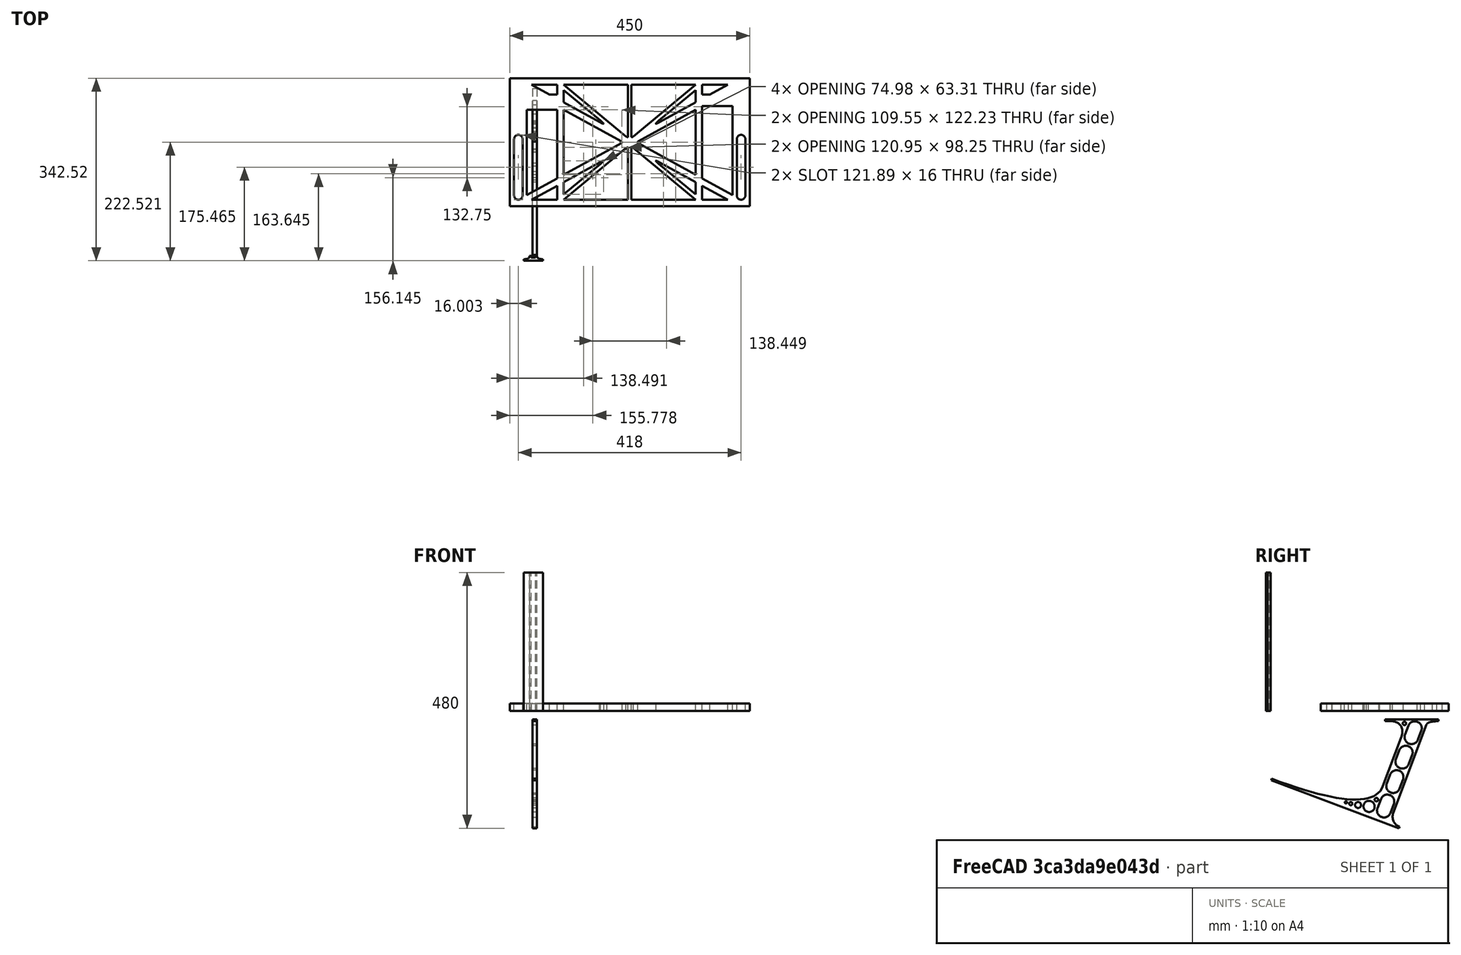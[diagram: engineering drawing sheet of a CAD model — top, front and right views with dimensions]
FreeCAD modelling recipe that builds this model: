
FCSTD DOCUMENT  (FreeCAD 0.19R0.19.2)
Label: laptopStand068
License: All rights reserved
LicenseURL: http://en.wikipedia.org/wiki/All_rights_reserved
objects: Sketcher::SketchObject×3, Part::Extrusion×3
note: 6 computed .brp shape members not serialized (recipe doc carries the construction recipe); baked Part::Feature solids carry a one-line shape summary decoded from their .brp

FEATURE [Sketcher::SketchObject] Sketch
  FullyConstrained = true
  sketch-geometry (126):
    g0: LineSegment StartX=-10.9272 StartY=-82.7794 StartZ=0 EndX=46.0728 EndY=-51.4823 EndZ=0
    g1: LineSegment StartX=366.073 StartY=-91.7794 StartZ=0 EndX=318.073 EndY=-65.424 EndZ=0
    g2: LineSegment StartX=-10.9272 StartY=77.3346 StartZ=0 EndX=-10.9272 EndY=-82.7794 EndZ=0
    g3: LineSegment StartX=375.073 StartY=-82.7794 StartZ=0 EndX=375.073 EndY=83.9235 EndZ=0
    g4: LineSegment StartX=-1.92719 StartY=-91.7794 StartZ=0 EndX=46.0728 EndY=-91.7794 EndZ=0
    g5: LineSegment StartX=318.073 StartY=124.221 StartZ=0 EndX=366.073 EndY=124.221 EndZ=0
    g6: LineSegment StartX=306.073 StartY=124.221 StartZ=0 EndX=189.124 EndY=27.0628 EndZ=0
    g7: LineSegment StartX=58.0728 StartY=-91.7794 StartZ=0 EndX=175.022 EndY=5.37834 EndZ=0
    g8: LineSegment StartX=58.0728 StartY=-81.8102 StartZ=0 EndX=58.0728 EndY=-58.8351 EndZ=0
    g9: LineSegment StartX=306.073 StartY=114.251 StartZ=0 EndX=306.073 EndY=91.2763 EndZ=0
    g10: LineSegment StartX=175.022 StartY=27.0628 StartZ=0 EndX=58.0728 EndY=124.221 EndZ=0
    g11: LineSegment StartX=139.632 StartY=-14.0532 StartZ=0 EndX=58.0728 EndY=-81.8102 EndZ=0
    g12: LineSegment StartX=139.632 StartY=-14.0532 StartZ=0 EndX=58.0728 EndY=-58.8351 EndZ=0
    g13: LineSegment StartX=189.124 StartY=5.37834 StartZ=0 EndX=306.073 EndY=-91.7794 EndZ=0
    g14: LineSegment StartX=306.073 StartY=77.3346 StartZ=0 EndX=306.073 EndY=-44.8935 EndZ=0
    g15: LineSegment StartX=318.073 StartY=83.9235 StartZ=0 EndX=318.073 EndY=-51.4823 EndZ=0
    g16: LineSegment StartX=306.073 StartY=-58.8351 StartZ=0 EndX=306.073 EndY=-81.8102 EndZ=0
    g17: LineSegment StartX=318.073 StartY=-51.4823 StartZ=0 EndX=375.073 EndY=-82.7794 EndZ=0
    g18: LineSegment StartX=318.073 StartY=-65.424 StartZ=0 EndX=318.073 EndY=-91.7794 EndZ=0
    g19: LineSegment StartX=318.073 StartY=-91.7794 StartZ=0 EndX=366.073 EndY=-91.7794 EndZ=0
    g20: LineSegment StartX=58.0728 StartY=-44.8935 StartZ=0 EndX=58.0728 EndY=77.3346 EndZ=0
    g21: LineSegment StartX=46.0728 StartY=-65.424 StartZ=0 EndX=-1.92719 EndY=-91.7794 EndZ=0
    g22: LineSegment StartX=46.0728 StartY=-65.424 StartZ=0 EndX=46.0728 EndY=-91.7794 EndZ=0
    g23: LineSegment StartX=58.0728 StartY=91.2763 StartZ=0 EndX=58.0728 EndY=114.251 EndZ=0
    g24: LineSegment StartX=46.0728 StartY=77.3346 StartZ=0 EndX=46.0728 EndY=-51.4823 EndZ=0
    g25: LineSegment StartX=-42.9272 StartY=136.221 StartZ=0 EndX=-42.9272 EndY=-103.779 EndZ=0
    g26: LineSegment StartX=407.073 StartY=136.221 StartZ=0 EndX=407.073 EndY=-103.779 EndZ=0
    g27: LineSegment StartX=179.022 StartY=27.0628 StartZ=0 EndX=179.022 EndY=124.221 EndZ=0
    g28: LineSegment StartX=185.124 StartY=27.0628 StartZ=0 EndX=185.124 EndY=124.221 EndZ=0
    g29: ArcOfCircle CenterX=-26.9272 CenterY=22.1087 CenterZ=0 NormalX=0 NormalY=0 NormalZ=1 AngleXU=0 Radius=8 StartAngle=1e-16 EndAngle=3.14159
    g30: ArcOfCircle CenterX=-26.9272 CenterY=-83.7794 CenterZ=0 NormalX=0 NormalY=0 NormalZ=1 AngleXU=0 Radius=8 StartAngle=3.14159 EndAngle=6.28319
    g31: LineSegment StartX=-34.9272 StartY=22.1087 StartZ=0 EndX=-34.9272 EndY=-83.7794 EndZ=0
    g32: LineSegment StartX=-18.9272 StartY=22.1087 StartZ=0 EndX=-18.9272 EndY=-83.7794 EndZ=0
    g33: LineSegment StartX=185.124 StartY=-91.7794 StartZ=0 EndX=306.073 EndY=-91.7794 EndZ=0
    g34: LineSegment StartX=179.022 StartY=-91.7794 StartZ=0 EndX=58.0728 EndY=-91.7794 EndZ=0
    g35: LineSegment StartX=306.073 StartY=124.221 StartZ=0 EndX=185.124 EndY=124.221 EndZ=0
    g36: LineSegment StartX=179.022 StartY=124.221 StartZ=0 EndX=58.0728 EndY=124.221 EndZ=0
    g37: ArcOfCircle CenterX=391.073 CenterY=22.1087 CenterZ=0 NormalX=0 NormalY=0 NormalZ=1 AngleXU=0 Radius=8 StartAngle=-4.4e-15 EndAngle=3.14159
    g38: LineSegment StartX=399.073 StartY=22.1087 StartZ=0 EndX=399.073 EndY=-83.7794 EndZ=0
    g39: LineSegment StartX=383.073 StartY=22.1087 StartZ=0 EndX=383.073 EndY=-83.7794 EndZ=0
    g40: ArcOfCircle CenterX=391.073 CenterY=-83.7794 CenterZ=0 NormalX=0 NormalY=0 NormalZ=1 AngleXU=0 Radius=8 StartAngle=3.14159 EndAngle=6.28319
    g41: Circle CenterX=175.022 CenterY=27.0628 CenterZ=0 NormalX=0 NormalY=0 NormalZ=1 AngleXU=0 Radius=1
    g42: Circle CenterX=179.022 CenterY=24.8665 CenterZ=0 NormalX=0 NormalY=0 NormalZ=1 AngleXU=0 Radius=1
    g43: Circle CenterX=179.022 CenterY=27.0628 CenterZ=0 NormalX=0 NormalY=0 NormalZ=1 AngleXU=0 Radius=1
    g44: BSplineCurve PolesCount=3 KnotsCount=2 Degree=2 IsPeriodic=0
    g45: GeomPoint X=175.022 Y=27.0628 Z=0
    g46: GeomPoint X=179.022 Y=27.0628 Z=0
    g47: Circle CenterX=189.124 CenterY=27.0628 CenterZ=0 NormalX=0 NormalY=0 NormalZ=1 AngleXU=0 Radius=1
    g48: Circle CenterX=185.124 CenterY=24.8665 CenterZ=0 NormalX=0 NormalY=0 NormalZ=1 AngleXU=0 Radius=1
    g49: Circle CenterX=185.124 CenterY=27.0628 CenterZ=0 NormalX=0 NormalY=0 NormalZ=1 AngleXU=0 Radius=1
    g50: BSplineCurve PolesCount=3 KnotsCount=2 Degree=2 IsPeriodic=0
    g51: GeomPoint X=189.124 Y=27.0628 Z=0
    g52: GeomPoint X=185.124 Y=27.0628 Z=0
    g53: Circle CenterX=175.022 CenterY=5.37834 CenterZ=0 NormalX=0 NormalY=0 NormalZ=1 AngleXU=0 Radius=1
    g54: Circle CenterX=179.022 CenterY=7.57463 CenterZ=0 NormalX=0 NormalY=0 NormalZ=1 AngleXU=0 Radius=1
    g55: Circle CenterX=179.022 CenterY=5.34704 CenterZ=0 NormalX=0 NormalY=0 NormalZ=1 AngleXU=0 Radius=1
    g56: BSplineCurve PolesCount=3 KnotsCount=2 Degree=2 IsPeriodic=0
    g57: GeomPoint X=175.022 Y=5.37834 Z=0
    g58: GeomPoint X=179.022 Y=5.34704 Z=0
    g59: Circle CenterX=189.124 CenterY=5.37834 CenterZ=0 NormalX=0 NormalY=0 NormalZ=1 AngleXU=0 Radius=1
    g60: Circle CenterX=185.124 CenterY=7.57463 CenterZ=0 NormalX=0 NormalY=0 NormalZ=1 AngleXU=0 Radius=1
    g61: Circle CenterX=185.124 CenterY=5.34704 CenterZ=0 NormalX=0 NormalY=0 NormalZ=1 AngleXU=0 Radius=1
    g62: BSplineCurve PolesCount=3 KnotsCount=2 Degree=2 IsPeriodic=0
    g63: GeomPoint X=189.124 Y=5.37834 Z=0
    g64: GeomPoint X=185.124 Y=5.34704 Z=0
    g65: LineSegment StartX=179.022 StartY=5.34704 StartZ=0 EndX=179.022 EndY=-91.7794 EndZ=0
    g66: LineSegment StartX=185.124 StartY=-91.7794 StartZ=0 EndX=185.124 EndY=5.34704 EndZ=0
    g67: Circle CenterX=165.871 CenterY=18.1458 CenterZ=0 NormalX=0 NormalY=0 NormalZ=1 AngleXU=0 Radius=1
    g68: Circle CenterX=169.377 CenterY=16.2206 CenterZ=0 NormalX=0 NormalY=0 NormalZ=1 AngleXU=0 Radius=1
    g69: Circle CenterX=165.871 CenterY=14.2954 CenterZ=0 NormalX=0 NormalY=0 NormalZ=1 AngleXU=0 Radius=1
    g70: BSplineCurve PolesCount=3 KnotsCount=2 Degree=2 IsPeriodic=0
    g71: GeomPoint X=165.871 Y=18.1458 Z=0
    g72: GeomPoint X=165.871 Y=14.2954 Z=0
    g73: Circle CenterX=198.275 CenterY=18.1458 CenterZ=0 NormalX=0 NormalY=0 NormalZ=1 AngleXU=0 Radius=1
    g74: Circle CenterX=194.768 CenterY=16.2206 CenterZ=0 NormalX=0 NormalY=0 NormalZ=1 AngleXU=0 Radius=1
    g75: Circle CenterX=198.275 CenterY=14.2954 CenterZ=0 NormalX=0 NormalY=0 NormalZ=1 AngleXU=0 Radius=1
    g76: BSplineCurve PolesCount=3 KnotsCount=2 Degree=2 IsPeriodic=0
    g77: GeomPoint X=198.275 Y=18.1458 Z=0
    g78: GeomPoint X=198.275 Y=14.2954 Z=0
    g79: LineSegment StartX=165.871 StartY=18.1458 StartZ=0 EndX=58.0728 EndY=77.3346 EndZ=0
    g80: LineSegment StartX=58.0728 StartY=-44.8935 StartZ=0 EndX=165.871 EndY=14.2954 EndZ=0
    g81: LineSegment StartX=198.275 StartY=18.1458 StartZ=0 EndX=306.073 EndY=77.3346 EndZ=0
    g82: LineSegment StartX=198.275 StartY=14.2954 StartZ=0 EndX=306.073 EndY=-44.8935 EndZ=0
    g83: LineSegment StartX=407.073 StartY=-103.779 StartZ=0 EndX=-42.9272 EndY=-103.779 EndZ=0
    g84: LineSegment StartX=407.073 StartY=136.221 StartZ=0 EndX=-42.9272 EndY=136.221 EndZ=0
    g85: LineSegment StartX=46.0728 StartY=77.3346 StartZ=0 EndX=-10.9272 EndY=77.3346 EndZ=0
    g86: LineSegment StartX=46.0728 StartY=105.865 StartZ=0 EndX=31.5028 EndY=105.865 EndZ=0
    g87: LineSegment StartX=46.0728 StartY=124.221 StartZ=0 EndX=46.0728 EndY=105.865 EndZ=0
    g88: LineSegment StartX=-1.92719 StartY=124.221 StartZ=0 EndX=31.5028 EndY=105.865 EndZ=0
    g89: LineSegment StartX=46.0728 StartY=124.221 StartZ=0 EndX=-1.92719 EndY=124.221 EndZ=0
    g90: LineSegment StartX=318.073 StartY=83.9235 StartZ=0 EndX=375.073 EndY=83.9235 EndZ=0
    g91: LineSegment StartX=318.073 StartY=105.865 StartZ=0 EndX=332.643 EndY=105.865 EndZ=0
    g92: LineSegment StartX=332.643 StartY=105.865 StartZ=0 EndX=366.073 EndY=124.221 EndZ=0
    g93: LineSegment StartX=318.073 StartY=124.221 StartZ=0 EndX=318.073 EndY=105.865 EndZ=0
    g94: Circle CenterX=125.607 CenterY=54.1951 CenterZ=0 NormalX=0 NormalY=0 NormalZ=1 AngleXU=0 Radius=1
    g95: Circle CenterX=139.632 CenterY=46.4944 CenterZ=0 NormalX=0 NormalY=0 NormalZ=1 AngleXU=0 Radius=1
    g96: Circle CenterX=127.325 CenterY=56.7187 CenterZ=0 NormalX=0 NormalY=0 NormalZ=1 AngleXU=0 Radius=1
    g97: BSplineCurve PolesCount=3 KnotsCount=2 Degree=2 IsPeriodic=0
    g98: GeomPoint X=125.607 Y=54.1951 Z=0
    g99: GeomPoint X=127.325 Y=56.7187 Z=0
    g100: LineSegment StartX=127.325 StartY=56.7187 StartZ=0 EndX=58.0728 EndY=114.251 EndZ=0
    g101: LineSegment StartX=58.0728 StartY=91.2763 StartZ=0 EndX=125.607 EndY=54.1951 EndZ=0
    g102: Circle CenterX=236.821 CenterY=56.7187 CenterZ=0 NormalX=0 NormalY=0 NormalZ=1 AngleXU=0 Radius=1
    g103: Circle CenterX=224.513 CenterY=46.4944 CenterZ=0 NormalX=0 NormalY=0 NormalZ=1 AngleXU=0 Radius=1
    g104: Circle CenterX=238.538 CenterY=54.1951 CenterZ=0 NormalX=0 NormalY=0 NormalZ=1 AngleXU=0 Radius=1
    g105: BSplineCurve PolesCount=3 KnotsCount=2 Degree=2 IsPeriodic=0
    g106: GeomPoint X=236.821 Y=56.7187 Z=0
    g107: GeomPoint X=238.538 Y=54.1951 Z=0
    g108: LineSegment StartX=236.821 StartY=56.7187 StartZ=0 EndX=306.073 EndY=114.251 EndZ=0
    g109: LineSegment StartX=238.538 StartY=54.1951 StartZ=0 EndX=306.073 EndY=91.2763 EndZ=0
    g110: Circle CenterX=238.538 CenterY=-21.7539 CenterZ=0 NormalX=0 NormalY=0 NormalZ=1 AngleXU=0 Radius=1
    g111: Circle CenterX=224.513 CenterY=-14.0532 CenterZ=0 NormalX=0 NormalY=0 NormalZ=1 AngleXU=0 Radius=1
    g112: Circle CenterX=236.821 CenterY=-24.2775 CenterZ=0 NormalX=0 NormalY=0 NormalZ=1 AngleXU=0 Radius=1
    g113: BSplineCurve PolesCount=3 KnotsCount=2 Degree=2 IsPeriodic=0
    g114: GeomPoint X=238.538 Y=-21.7539 Z=0
    g115: GeomPoint X=236.821 Y=-24.2775 Z=0
    g116: LineSegment StartX=238.538 StartY=-21.7539 StartZ=0 EndX=306.073 EndY=-58.8351 EndZ=0
    g117: LineSegment StartX=236.821 StartY=-24.2775 StartZ=0 EndX=306.073 EndY=-81.8102 EndZ=0
    g118: LineSegment StartX=139.632 StartY=-14.0532 StartZ=0 EndX=125.607 EndY=-21.7539 EndZ=0
    g119: LineSegment StartX=139.632 StartY=-14.0532 StartZ=0 EndX=127.325 EndY=-24.2775 EndZ=0
    g120: Circle CenterX=125.607 CenterY=-21.7539 CenterZ=0 NormalX=0 NormalY=0 NormalZ=1 AngleXU=0 Radius=1
    g121: Circle CenterX=139.632 CenterY=-14.0532 CenterZ=0 NormalX=0 NormalY=0 NormalZ=1 AngleXU=0 Radius=1
    g122: Circle CenterX=127.325 CenterY=-24.2775 CenterZ=0 NormalX=0 NormalY=0 NormalZ=1 AngleXU=0 Radius=1
    g123: BSplineCurve PolesCount=3 KnotsCount=2 Degree=2 IsPeriodic=0
    g124: GeomPoint X=125.607 Y=-21.7539 Z=0
    g125: GeomPoint X=127.325 Y=-24.2775 Z=0
  constraints (233):
    c: Horizontal(g4)
    c: Horizontal(g5)
    c: Coincident(g12,g11)
    c: Tangent(g9,g14)
    c: Tangent(g14,g16)
    c: Coincident(g15,g17)
    c: Coincident(g18,g1)
    c: Tangent(g15,g18)
    c: Coincident(g11,g8)
    c: Tangent(g8,g20)
    c: Coincident(g12,g8)
    c: Tangent(g12,g21)
    c: Coincident(g22,g21)
    c: Coincident(g0,g24)
    c: Tangent(g20,g23)
    c: Block(g10)
    c: Block(g6)
    c: Block(g17)
    c: Block(g3)
    c: Block(g16)
    c: Block(g1)
    c: Block(g18)
    c: Block(g13)
    c: Block(g7)
    c: Block(g12)
    c: Block(g11)
    c: Block(g22)
    c: Block(g21)
    c: Block(g0)
    c: Block(g2)
    c: Block(g23)
    c: Block(g14)
    c: Block(g5)
    c: Block(g19)
    c: Block(g4)
    c: Vertical(g25)
    c: Vertical(g26)
    c: Block(g26)
    c: Block(g25)
    c: Vertical(g27)
    c: Vertical(g28)
    c: Block(g27)
    c: Block(g28)
    c: Tangent(g29,g32) = 1.5708
    c: Tangent(g29,g31) = -1.5708
    c: Tangent(g31,g30) = -1.5708
    c: Tangent(g32,g30) = 1.5708
    c: Vertical(g31)
    c: Equal(g29,g30)
    c: Block(g32)
    c: Block(g31)
    c: Coincident(g33,g13)
    c: Horizontal(g33)
    c: Coincident(g34,g7)
    c: Horizontal(g34)
    c: Coincident(g35,g6)
    c: Coincident(g35,g28)
    c: Horizontal(g35)
    c: Coincident(g36,g27)
    c: Coincident(g36,g10)
    c: Horizontal(g36)
    c: Tangent(g37,g38) = 1.5708
    c: Tangent(g38,g40) = 1.5708
    c: Equal(g37,g40)
    c: Coincident(g39,g37)
    c: Coincident(g39,g40)
    c: Block(g38)
    c: Block(g39)
    c: Coincident(g44,g10)
    c: Weight(g41) = 1
    c: Equal(g41,g42)
    c: Equal(g41,g43)
    c: Coincident(g44,g27)
    c: InternalAlignment(g41,g44)
    c: InternalAlignment(g42,g44)
    c: InternalAlignment(g43,g44)
    c: InternalAlignment(g45,g44)
    c: InternalAlignment(g46,g44)
    c: Coincident(g50,g6)
    c: Weight(g47) = 1
    c: Equal(g47,g48)
    c: Equal(g47,g49)
    c: Coincident(g50,g28)
    c: InternalAlignment(g47,g50)
    c: InternalAlignment(g48,g50)
    c: InternalAlignment(g49,g50)
    c: InternalAlignment(g51,g50)
    c: InternalAlignment(g52,g50)
    c: Block(g50)
    c: Block(g44)
    c: Coincident(g56,g7)
    c: Weight(g53) = 1
    c: Equal(g53,g54)
    c: Equal(g53,g55)
    c: InternalAlignment(g53,g56)
    c: InternalAlignment(g54,g56)
    c: InternalAlignment(g55,g56)
    c: InternalAlignment(g57,g56)
    c: InternalAlignment(g58,g56)
    c: Weight(g59) = 1
    c: Equal(g59,g60)
    c: Equal(g59,g61)
    c: InternalAlignment(g59,g62)
    c: InternalAlignment(g60,g62)
    c: InternalAlignment(g61,g62)
    c: InternalAlignment(g63,g62)
    c: InternalAlignment(g64,g62)
    c: Block(g62)
    c: Block(g56)
    c: Coincident(g65,g56)
    c: Coincident(g65,g34)
    c: Vertical(g65)
    c: Coincident(g66,g33)
    c: Coincident(g66,g62)
    c: Vertical(g66)
    c: Weight(g67) = 1
    c: Equal(g67,g68)
    c: Equal(g67,g69)
    c: InternalAlignment(g67,g70)
    c: InternalAlignment(g68,g70)
    c: InternalAlignment(g69,g70)
    c: InternalAlignment(g71,g70)
    c: InternalAlignment(g72,g70)
    c: Weight(g73) = 1
    c: Equal(g73,g74)
    c: Equal(g73,g75)
    c: InternalAlignment(g73,g76)
    c: InternalAlignment(g74,g76)
    c: InternalAlignment(g75,g76)
    c: InternalAlignment(g77,g76)
    c: InternalAlignment(g78,g76)
    c: Block(g70)
    c: Block(g76)
    c: Coincident(g79,g70)
    c: Coincident(g79,g20)
    c: Coincident(g80,g20)
    c: Coincident(g80,g70)
    c: Coincident(g81,g76)
    c: Coincident(g81,g14)
    c: Coincident(g82,g76)
    c: Coincident(g82,g14)
    c: Block(g20)
    c: Coincident(g83,g26)
    c: Coincident(g83,g25)
    c: Horizontal(g83)
    c: Distance(g83) = 450
    c: Coincident(g84,g26)
    c: Coincident(g84,g25)
    c: Horizontal(g84)
    c: Horizontal(g85)
    c: Coincident(g24,g85)
    c: Horizontal(g86)
    c: Vertical(g87)
    c: Block(g87)
    c: Block(g86)
    c: Block(g85)
    c: Distance(g87) = 18.3554
    c: Coincident(g89,g87)
    c: Coincident(g89,g88)
    c: Horizontal(g89)
    c: Block(g89)
    c: Block(g88)
    c: Coincident(g86,g88)
    c: Coincident(g2,g85)
    c: Coincident(g90,g15)
    c: Horizontal(g90)
    c: Horizontal(g91)
    c: Block(g90)
    c: Block(g9)
    c: Coincident(g92,g5)
    c: Coincident(g93,g5)
    c: Coincident(g93,g91)
    c: Vertical(g93)
    c: Block(g93)
    c: Coincident(g91,g92)
    c: Block(g92)
    c: Coincident(g3,g90)
    c: Weight(g94) = 1
    c: Equal(g94,g95)
    c: Equal(g94,g96)
    c: InternalAlignment(g94,g97)
    c: InternalAlignment(g95,g97)
    c: InternalAlignment(g96,g97)
    c: InternalAlignment(g98,g97)
    c: InternalAlignment(g99,g97)
    c: Block(g97)
    c: Coincident(g100,g97)
    c: Coincident(g100,g23)
    c: Coincident(g101,g23)
    c: Coincident(g101,g97)
    c: Weight(g102) = 1
    c: Equal(g102,g103)
    c: Equal(g102,g104)
    c: InternalAlignment(g102,g105)
    c: InternalAlignment(g103,g105)
    c: InternalAlignment(g104,g105)
    c: InternalAlignment(g106,g105)
    c: InternalAlignment(g107,g105)
    c: Block(g105)
    c: Coincident(g108,g105)
    c: Coincident(g108,g9)
    c: Coincident(g109,g105)
    c: Coincident(g109,g9)
    c: Weight(g110) = 1
    c: Equal(g110,g111)
    c: Equal(g110,g112)
    c: InternalAlignment(g110,g113)
    c: InternalAlignment(g111,g113)
    c: InternalAlignment(g112,g113)
    c: InternalAlignment(g114,g113)
    c: InternalAlignment(g115,g113)
    c: Block(g113)
    c: Coincident(g116,g113)
    c: Coincident(g116,g16)
    c: Coincident(g117,g113)
    c: Coincident(g117,g16)
    c: Distance(g118) = 16
    c: Coincident(g118,g11)
    c: Coincident(g119,g11)
    c: Distance(g119) = 16
    c: Parallel(g119,g11)
    c: Parallel(g12,g118)
    c: Coincident(g123,g118)
    c: Weight(g120) = 1
    c: Equal(g120,g121)
    c: Coincident(g121,g11)
    c: Equal(g120,g122)
    c: Coincident(g123,g119)
    c: InternalAlignment(g120,g123)
    c: InternalAlignment(g121,g123)
    c: InternalAlignment(g122,g123)
    c: InternalAlignment(g124,g123)
    c: InternalAlignment(g125,g123)
FEATURE [Sketcher::SketchObject] Sketch001
  FullyConstrained = true
  MapMode = 4
  Placement = pos=(0,0,0) rot=(0.57735,0.57735,0.57735;2.0944rad)
  Support = -> [Sketch]
  sketch-geometry (46):
    g0: BSplineCurve PolesCount=3 KnotsCount=2 Degree=2 IsPeriodic=0
    g1: ArcOfCircle CenterX=73.1223 CenterY=-32.291 CenterZ=0 NormalX=0 NormalY=0 NormalZ=1 AngleXU=0 Radius=13 StartAngle=5.92268 EndAngle=9.06428
    g2: ArcOfCircle CenterX=66.7816 CenterY=-49.1439 CenterZ=0 NormalX=0 NormalY=0 NormalZ=1 AngleXU=0 Radius=13 StartAngle=2.78068 EndAngle=5.92131
    g3: ArcOfCircle CenterX=55.9263 CenterY=-78.1807 CenterZ=0 NormalX=0 NormalY=0 NormalZ=1 AngleXU=0 Radius=13 StartAngle=5.92268 EndAngle=9.06428
    g4: ArcOfCircle CenterX=49.5884 CenterY=-95.0342 CenterZ=0 NormalX=0 NormalY=0 NormalZ=1 AngleXU=0 Radius=13 StartAngle=2.78068 EndAngle=5.92131
    g5: ArcOfCircle CenterX=38.7206 CenterY=-124.067 CenterZ=0 NormalX=0 NormalY=0 NormalZ=1 AngleXU=0 Radius=13 StartAngle=5.92268 EndAngle=9.06428
    g6: ArcOfCircle CenterX=32.3875 CenterY=-140.92 CenterZ=0 NormalX=0 NormalY=0 NormalZ=1 AngleXU=0 Radius=13 StartAngle=2.78068 EndAngle=5.92131
    g7: ArcOfCircle CenterX=21.4715 CenterY=-169.934 CenterZ=0 NormalX=0 NormalY=0 NormalZ=1 AngleXU=0 Radius=13 StartAngle=5.92268 EndAngle=9.06428
    g8: ArcOfCircle CenterX=15.1336 CenterY=-186.787 CenterZ=0 NormalX=0 NormalY=0 NormalZ=1 AngleXU=0 Radius=13 StartAngle=2.78068 EndAngle=5.92131
    g9-g12: Circle x4 (B-spline internal-alignment scaffolding for g13; pole/knot coordinates omitted)
    g13: BSplineCurve PolesCount=4 KnotsCount=2 Degree=3 IsPeriodic=0
    g14: GeomPoint X=28.8094 Y=-19.0875 Z=0
    g15: GeomPoint X=47.0443 Y=-50.4712 Z=0
    g16: Circle CenterX=53.5586 CenterY=-23.2695 CenterZ=0 NormalX=0 NormalY=0 NormalZ=1 AngleXU=0 Radius=3.24518
    g17: Circle CenterX=-195.441 CenterY=-127.082 CenterZ=0 NormalX=0 NormalY=0 NormalZ=1 AngleXU=0 Radius=1
    g18: Circle CenterX=-8.24091 CenterY=-197.481 CenterZ=0 NormalX=0 NormalY=0 NormalZ=1 AngleXU=0 Radius=1
    g19: Circle CenterX=12.8789 CenterY=-141.321 CenterZ=0 NormalX=0 NormalY=0 NormalZ=1 AngleXU=0 Radius=1
    g20: BSplineCurve PolesCount=3 KnotsCount=2 Degree=2 IsPeriodic=0
    g21: GeomPoint X=-195.441 Y=-127.082 Z=0
    g22: GeomPoint X=12.8789 Y=-141.321 Z=0
    g23: Circle CenterX=-12.8016 CenterY=-179.036 CenterZ=0 NormalX=0 NormalY=0 NormalZ=1 AngleXU=0 Radius=10.5072
    g24: Circle CenterX=0.933922 CenterY=-166.43 CenterZ=0 NormalX=0 NormalY=0 NormalZ=1 AngleXU=0 Radius=3.26661
    g25: Circle CenterX=-33.5518 CenterY=-176.44 CenterZ=0 NormalX=0 NormalY=0 NormalZ=1 AngleXU=0 Radius=5.64388
    g26: Circle CenterX=-47.2366 CenterY=-173.859 CenterZ=0 NormalX=0 NormalY=0 NormalZ=1 AngleXU=0 Radius=3.01653
    g27: Circle CenterX=-56.2595 CenterY=-171.456 CenterZ=0 NormalX=0 NormalY=0 NormalZ=1 AngleXU=0 Radius=2.12826
    g28: ArcOfCircle CenterX=51.2151 CenterY=-198.473 CenterZ=0 NormalX=0 NormalY=0 NormalZ=1 AngleXU=0 Radius=20 StartAngle=2.78189 EndAngle=4.35269
    g29: LineSegment StartX=32.4951 StartY=-191.433 StartZ=0 EndX=94.6578 EndY=-26.1352 EndZ=0
    g30: LineSegment StartX=43.1192 StartY=-220.001 StartZ=0 EndX=-196.497 EndY=-129.89 EndZ=0
    g31: LineSegment StartX=43.1192 StartY=-220.001 StartZ=0 EndX=44.1752 EndY=-217.193 EndZ=0
    g32: LineSegment StartX=117.223 StartY=-19.0875 StartZ=0 EndX=117.223 EndY=-16.0875 EndZ=0
    g33: LineSegment StartX=117.223 StartY=-16.0875 StartZ=0 EndX=17.2232 EndY=-16.0875 EndZ=0
    g34: LineSegment StartX=17.2232 StartY=-16.0875 StartZ=0 EndX=17.2232 EndY=-19.0875 EndZ=0
    g35: LineSegment StartX=28.8094 StartY=-19.0875 StartZ=0 EndX=17.2232 EndY=-19.0875 EndZ=0
    g36: LineSegment StartX=47.0443 StartY=-50.4712 StartZ=0 EndX=12.8789 EndY=-141.321 EndZ=0
    g37: LineSegment StartX=-195.441 StartY=-127.082 StartZ=0 EndX=-196.497 EndY=-129.89 EndZ=0
    g38: LineSegment StartX=85.2866 StartY=-36.8766 StartZ=0 EndX=78.9396 EndY=-53.7463 EndZ=0
    g39: LineSegment StartX=60.9579 StartY=-27.7053 StartZ=0 EndX=54.6191 EndY=-44.5532 EndZ=0
    g40: LineSegment StartX=68.0907 StartY=-82.7664 StartZ=0 EndX=61.7465 EndY=-99.6365 EndZ=0
    g41: LineSegment StartX=43.7619 StartY=-73.595 StartZ=0 EndX=37.426 EndY=-90.4435 EndZ=0
    g42: LineSegment StartX=50.885 StartY=-128.652 StartZ=0 EndX=44.5456 EndY=-145.522 EndZ=0
    g43: LineSegment StartX=26.5562 StartY=-119.481 StartZ=0 EndX=20.2251 EndY=-136.329 EndZ=0
    g44: LineSegment StartX=9.3071 StartY=-165.349 StartZ=0 EndX=2.97115 EndY=-182.197 EndZ=0
    g45: LineSegment StartX=33.6358 StartY=-174.52 StartZ=0 EndX=27.2917 EndY=-191.39 EndZ=0
  constraints (71):
    c: Block(g0)
    c: Block(g1)
    c: Block(g2)
    c: Block(g4)
    c: Block(g3)
    c: Block(g6)
    c: Block(g5)
    c: Block(g8)
    c: Block(g7)
    c: Weight(g9) = 1
    c: Equal(g9,g10)
    c: Equal(g9,g11)
    c: Equal(g9,g12)
    c: InternalAlignment(g9-g12 -> g13) x4
    c: InternalAlignment(g14,g13)
    c: InternalAlignment(g15,g13)
    c: Block(g16)
    c: Weight(g17) = 1
    c: Equal(g17,g18)
    c: Equal(g17,g19)
    c: InternalAlignment(g17,g20)
    c: InternalAlignment(g18,g20)
    c: InternalAlignment(g19,g20)
    c: InternalAlignment(g21,g20)
    c: InternalAlignment(g22,g20)
    c: Block(g20)
    c: Block(g23)
    c: Block(g24)
    c: Block(g25)
    c: Block(g26)
    c: Block(g27)
    c: Block(g28)
    c: Coincident(g29,g28)
    c: Coincident(g29,g0)
    c: Block(g13)
    c: Coincident(g31,g30)
    c: Coincident(g31,g28)
    c: Block(g31)
    c: Coincident(g32,g0)
    c: Vertical(g32)
    c: Coincident(g33,g32)
    c: Horizontal(g33)
    c: Coincident(g34,g33)
    c: Vertical(g34)
    c: Block(g33)
    c: Coincident(g35,g13)
    c: Coincident(g35,g34)
    c: Horizontal(g35)
    c: Coincident(g36,g13)
    c: Coincident(g36,g20)
    c: Coincident(g37,g20)
    c: Coincident(g37,g30)
    c: Block(g30)
    c: Coincident(g38,g1)
    c: Coincident(g38,g2)
    c: Coincident(g39,g1)
    c: Coincident(g39,g2)
    c: Coincident(g40,g3)
    c: Coincident(g40,g4)
    c: Coincident(g41,g3)
    c: Coincident(g41,g4)
    c: Coincident(g42,g5)
    c: Coincident(g42,g6)
    c: Coincident(g43,g5)
    c: Coincident(g43,g6)
    c: Coincident(g44,g7)
    c: Coincident(g44,g8)
    c: Coincident(g45,g7)
    c: Coincident(g45,g8)
    c: Distance(g30) = 256
    c: Distance(g33) = 100
FEATURE [Part::Extrusion] Extrude002
  Base = -> Sketch001
  Dir = (1,0,0)
  DirMode = 2
  FaceMakerClass = Part::FaceMakerBullseye
  LengthFwd = 8
  LengthRev = 0
  Solid = true
  Symmetric = false
FEATURE [Sketcher::SketchObject] Sketch002
  FullyConstrained = true
  sketch-geometry (20):
    g0: LineSegment StartX=-2.77179 StartY=-200.304 StartZ=0 EndX=5.22821 EndY=-200.304 EndZ=0
    g1: LineSegment StartX=5.22821 StartY=-200.304 StartZ=0 EndX=5.22821 EndY=-197.304 EndZ=0
    g2: LineSegment StartX=-2.77179 StartY=-200.304 StartZ=0 EndX=-2.77179 EndY=-197.304 EndZ=0
    g3: LineSegment StartX=5.22821 StartY=-197.304 StartZ=0 EndX=8.22821 EndY=-197.304 EndZ=0
    g4: LineSegment StartX=-2.77179 StartY=-197.304 StartZ=0 EndX=-5.77179 EndY=-197.304 EndZ=0
    g5: LineSegment StartX=19.2282 StartY=-203.304 StartZ=0 EndX=19.2282 EndY=-206.304 EndZ=0
    g6: LineSegment StartX=-16.7718 StartY=-203.304 StartZ=0 EndX=-16.7718 EndY=-206.304 EndZ=0
    g7: LineSegment StartX=-16.7718 StartY=-206.304 StartZ=0 EndX=19.2282 EndY=-206.304 EndZ=0
    g8: Circle CenterX=-16.7718 CenterY=-203.304 CenterZ=0 NormalX=0 NormalY=0 NormalZ=1 AngleXU=0 Radius=1
    g9: Circle CenterX=-5.77179 CenterY=-203.304 CenterZ=0 NormalX=0 NormalY=0 NormalZ=1 AngleXU=0 Radius=1
    g10: Circle CenterX=-5.77179 CenterY=-197.304 CenterZ=0 NormalX=0 NormalY=0 NormalZ=1 AngleXU=0 Radius=1
    g11: BSplineCurve PolesCount=3 KnotsCount=2 Degree=2 IsPeriodic=0
    g12: GeomPoint X=-16.7718 Y=-203.304 Z=0
    g13: GeomPoint X=-5.77179 Y=-197.304 Z=0
    g14: Circle CenterX=19.2282 CenterY=-203.304 CenterZ=0 NormalX=0 NormalY=0 NormalZ=1 AngleXU=0 Radius=1
    g15: Circle CenterX=8.22821 CenterY=-203.304 CenterZ=0 NormalX=0 NormalY=0 NormalZ=1 AngleXU=0 Radius=1
    g16: Circle CenterX=8.22821 CenterY=-197.304 CenterZ=0 NormalX=0 NormalY=0 NormalZ=1 AngleXU=0 Radius=1
    g17: BSplineCurve PolesCount=3 KnotsCount=2 Degree=2 IsPeriodic=0
    g18: GeomPoint X=19.2282 Y=-203.304 Z=0
    g19: GeomPoint X=8.22821 Y=-197.304 Z=0
  constraints (41):
    c: Horizontal(g0)
    c: Distance(g0) = 8
    c: Coincident(g1,g0)
    c: Vertical(g1)
    c: Distance(g1) = 3
    c: Coincident(g2,g0)
    c: Vertical(g2)
    c: Distance(g2) = 3
    c: Coincident(g3,g1)
    c: Horizontal(g3)
    c: Distance(g3) = 3
    c: Coincident(g4,g2)
    c: Horizontal(g4)
    c: Distance(g4) = 3
    c: Vertical(g5)
    c: Vertical(g6)
    c: Coincident(g7,g6)
    c: Coincident(g7,g5)
    c: Weight(g8) = 1
    c: Equal(g8,g9)
    c: Equal(g8,g10)
    c: Coincident(g11,g4)
    c: InternalAlignment(g8,g11)
    c: InternalAlignment(g9,g11)
    c: InternalAlignment(g10,g11)
    c: InternalAlignment(g12,g11)
    c: InternalAlignment(g13,g11)
    c: Coincident(g17,g5)
    c: Weight(g14) = 1
    c: Equal(g14,g15)
    c: Equal(g14,g16)
    c: Coincident(g17,g3)
    c: InternalAlignment(g14,g17)
    c: InternalAlignment(g15,g17)
    c: InternalAlignment(g16,g17)
    c: InternalAlignment(g18,g17)
    c: InternalAlignment(g19,g17)
    c: Block(g7)
    c: Block(g17)
    c: Block(g11)
    c: Block(g6)
FEATURE [Part::Extrusion] Extrude003
  Base = -> Sketch002
  Dir = (0,0,1)
  DirMode = 2
  FaceMakerClass = Part::FaceMakerBullseye
  LengthFwd = 260
  LengthRev = 0
  Solid = true
  Symmetric = false
FEATURE [Part::Extrusion] Extrude
  Base = -> Sketch
  Dir = (0,0,1)
  DirMode = 2
  FaceMakerClass = Part::FaceMakerBullseye
  LengthFwd = 14
  LengthRev = 0
  Solid = true
  Symmetric = false
